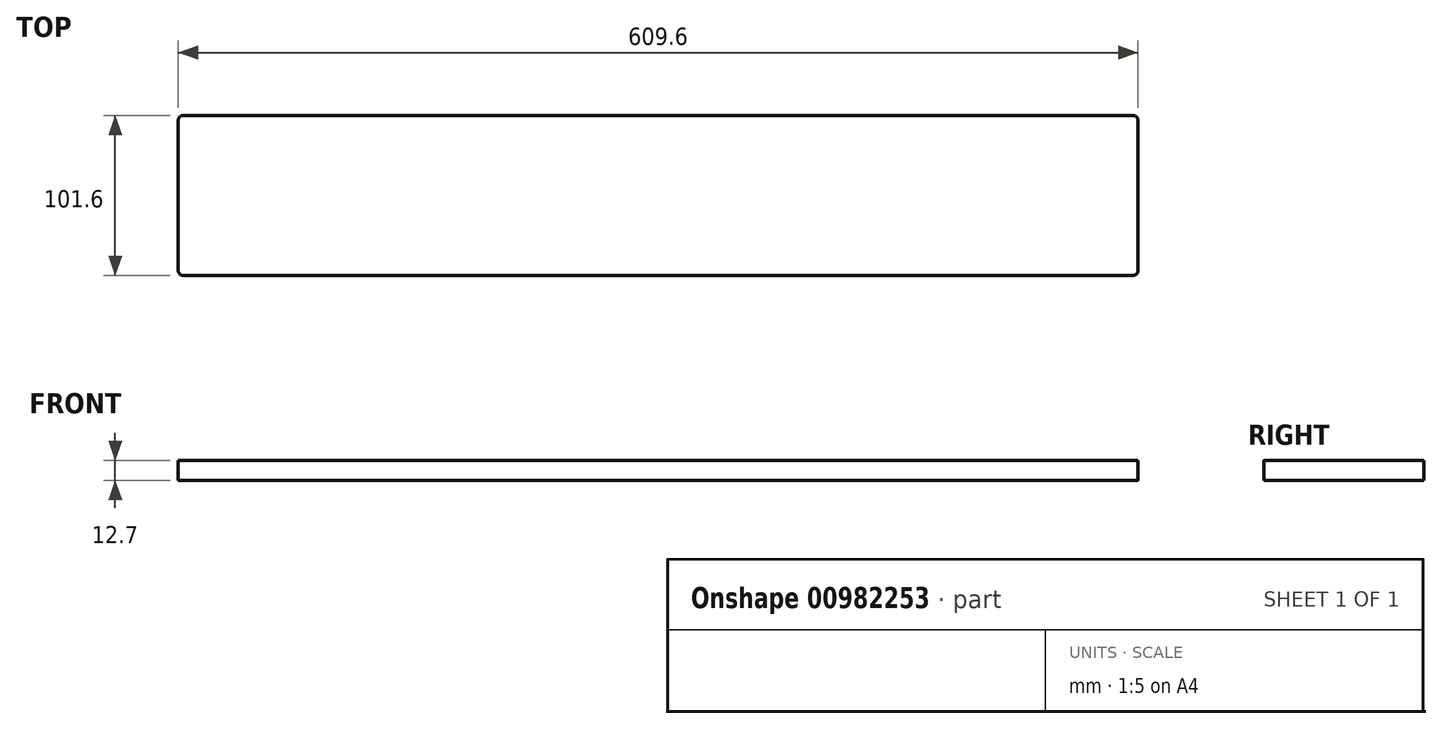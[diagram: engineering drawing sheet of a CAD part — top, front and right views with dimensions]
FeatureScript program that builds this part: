
annotation { "Feature Type Name" : "Feature", "Feature Type Description" : "" }
export const myFeature = defineFeature(function(context is Context, id is Id, definition is map)
    precondition{}
    {
        {
            var Q0;
            Q0=qCreatedBy(makeId("Top.planeOp"),FACE);
            var sketch = newSketch(context, id + "F0", { "sketchPlane" : qUnion([Q0])});
            skLineSegment(sketch, "E0.bottom", {"start": v(301.63, -50.8) * mm, "end": v(-301.63, -50.8) * mm});
            skLineSegment(sketch, "E0.top", {"start": v(301.63, 50.8) * mm, "end": v(-301.63, 50.8) * mm});
            skLineSegment(sketch, "E0.left", {"start": v(304.8, -47.62) * mm, "end": v(304.8, 47.63) * mm});
            skLineSegment(sketch, "E0.right", {"start": v(-304.8, -47.63) * mm, "end": v(-304.8, 47.63) * mm});
            skPoint(sketch, "E0.middle", {"position": v(0, 0) * mm});
            skPoint(sketch, "E1.visualSharp", {"position": v(304.8, 50.8) * mm});
            skArc(sketch, "E1.filletArc", {"start": v(304.8, 47.63) * mm, "mid": v(303.87, 49.87) * mm, "end": v(301.63, 50.8) * mm});
            skPoint(sketch, "E2.visualSharp", {"position": v(304.8, -50.8) * mm});
            skArc(sketch, "E2.filletArc", {"start": v(301.63, -50.8) * mm, "mid": v(303.87, -49.87) * mm, "end": v(304.8, -47.62) * mm});
            skPoint(sketch, "E3.visualSharp", {"position": v(-304.8, -50.8) * mm});
            skArc(sketch, "E3.filletArc", {"start": v(-304.8, -47.63) * mm, "mid": v(-303.87, -49.87) * mm, "end": v(-301.63, -50.8) * mm});
            skPoint(sketch, "E4.visualSharp", {"position": v(-304.8, 50.8) * mm});
            skArc(sketch, "E4.filletArc", {"start": v(-301.63, 50.8) * mm, "mid": v(-303.87, 49.87) * mm, "end": v(-304.8, 47.63) * mm});
            skSolve(sketch);
        }
        {
            var Q0;
            Q0 = qSketchRegion(id + "F0", true);
            extrude(context, id + "F1", {"entities" : qUnion([Q0]), "depth" : 12.7 * mm, "offsetDistance" : 25.4 * mm});
        }
    });
